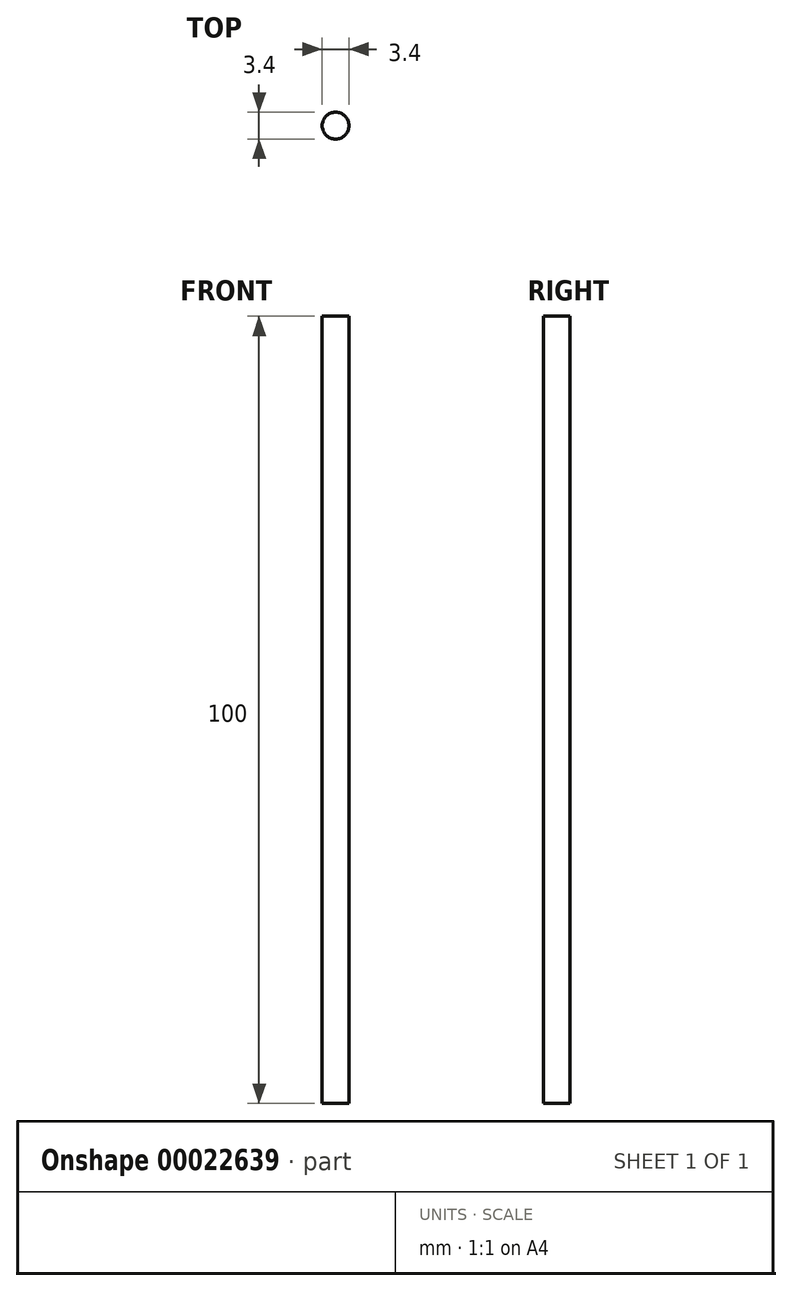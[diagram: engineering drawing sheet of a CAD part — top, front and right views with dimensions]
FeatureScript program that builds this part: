
annotation { "Feature Type Name" : "Feature", "Feature Type Description" : "" }
export const myFeature = defineFeature(function(context is Context, id is Id, definition is map)
    precondition{}
    {
        {
            var Q0;
            Q0=qCreatedBy(makeId("Top.planeOp"),FACE);
            var sketch = newSketch(context, id + "F0", { "sketchPlane" : qUnion([Q0])});
            skCircle(sketch, "E0", {"center": v(0, 0) * mm, "radius": 1.7 * mm});
            skSolve(sketch);
        }
        {
            var Q0;
            Q0 = qSketchRegion(id + "F0", true);
            var Q1;
            Q1=makeQuery(id+"F0.imprint","IMPRINT",FACE,{"disambiguationData":[TD([[makeQuery(id+"F0.imprint","IMPRINT",EDGE,{"derivedFrom":sQuery(id+"F0.wireOp",EDGE,"E0")}),1.0]])]});
            extrude(context, id + "F1", {"entities" : qUnion([Q0, Q1]), "depth" : 100 * mm});
        }
    });
